# Revit family: PRD_FrankeWS_WlHngWshBsns_ClassroomBasin_ANMW322_ANMW323
name_source: partatom
category: Plumbing Fixtures
revit_build: Autodesk Revit 2018 (Build: 20190510_1515(x64)
units: mm (PartAtom-declared; Revit-internal decimal feet)

## family parameters
Cut with Voids When Loaded = Yes
Host = Face
OmniClass Number = 23.45.05.14.14.27
OmniClass Title = Service Sinks
Part Type = Normal
Room Calculation Point = No
Round Connector Dimension = Use Diameter
Shared = Yes

## types (2) — shared parameters
AssetType = Fixed
BowlConstruction = Radius corners
BowlDepth = 280.00 mm
BowlMaterial = PRD_AR_ResinBondedMaterial_White
BowlPosition = Right
BowlWidth = 440.00 mm
Brushes = Without brushes
Category = Pr_40_20_96_96, Wall-hung washbasins
Color = alpine white
Default Elevation = 750 mm  [stored 2.46063 ft]
DiameterNominal = 32  [stored 0.104987 ft]
DrainSize = 32 mm  [stored 0.104987 ft]
DrainerOrStorage = No
DurationUnit = year
Features = resin-bonded mineral material, alpine white colour
Finish = Coated
Grid = No
IfcExportAs = IfcSanitaryTerminalType
IfcExportType = WASHHANDBASIN
InletSize = DN 32
IntegralAccessories = incl. fixing material
Manufacturer = KWC Group AG
ManufacturerName = KWC Group AG
ManufacturerURL = www.kwc.com
Material = mineral material
MaterialCode = Miranit
NBSDescription = Wall hung wash basins
NBSReference = 45-35-70/369
NominalDepth = 450 mm  [stored 1.47638 ft]
NominalHeight = 150 mm
NominalWidth = 600 mm
NumberOfWashPlaces = 1
NumberOfWasteHoles = 1
OutletSize = DN 32
Overflow = No
ProductInformation = https://pim.kwc.com
RearUpstand = Yes
Shape = Cuboid
Size = 600 x 150 x 450 mm (W x H x D)
Spillway = No
Splashback = No
Sump = No
SumpBasket = No
TapLedge = Yes
TypeOfMounting = Wall mounting
TypeOfUtilitySink = Multi purpose sink
TypeOfWasteKit = Perforated waste
URL = www.kwc.com
Uniclass2015Code = Pr_40_20_96_96
Uniclass2015Title = Wall-hung washbasins
Uniclass2015Version = Products v1.17
Version = 1
WarrantyDurationUnit = year
WashRiffle = No
WasteHolePosition = Center
WasteHoleProjection = 220.00 mm
WasteKitIncluded = Yes
WasteSize = DN 32
zero-valued in all types: MountingOffset

## per-type parameters (varying)
| type | BIMObjectName | Description | GrossWeight | ModelNumber | Name | NetWeight | TapHole | TapHoleDiameter | TapHolePosition |
| ANMW322 | PRD_AR_WallHungWashbasins_ClassroomBasin_ANMW322 | Classroom sink made of resin-bonded mineral material with smooth, pore-free surface (temperature resistant up to 80°C). Colour Alpine White. With seamless bowl, without overflow, with tap landing and tap hole, sponge tray on the left side, front slightly arched. Rear contoured edge. Strainer waste DN 32, plastic threaded connection, fixing material included. | 25.00 kg | 2000106177 | Classroom Basin ANMW322 | 23.75 kg | Yes | 35.00 mm | Middle |
| ANMW323 | PRD_AR_WallHungWashbasins_ClassroomBasin_ANMW323 | Classroom sink made of resin-bonded mineral material with smooth, pore-free surface (temperature resistant up to 80°C). Colour Alpine White. With seamless bowl, without overflow, with tap landing, without tap hole, sponge tray on the left side. Front slightly arched. Rear contoured edge. Strainer waste DN 32, plastic threaded connection, fixing material included. | 26.00 kg | 2030006863 | Classroom Basin ANMW323 | 23.60 kg | No |  |  |

note: column(s) folded — value = type name in every type: Model, ModelReference

note: [stored X ft] marks values corroborated as IEEE doubles in the binary element streams (Revit-internal decimal feet)

## geometry (parser evidence)
native form markers: Sweep x5
no freeform markers — native parametric forms only
